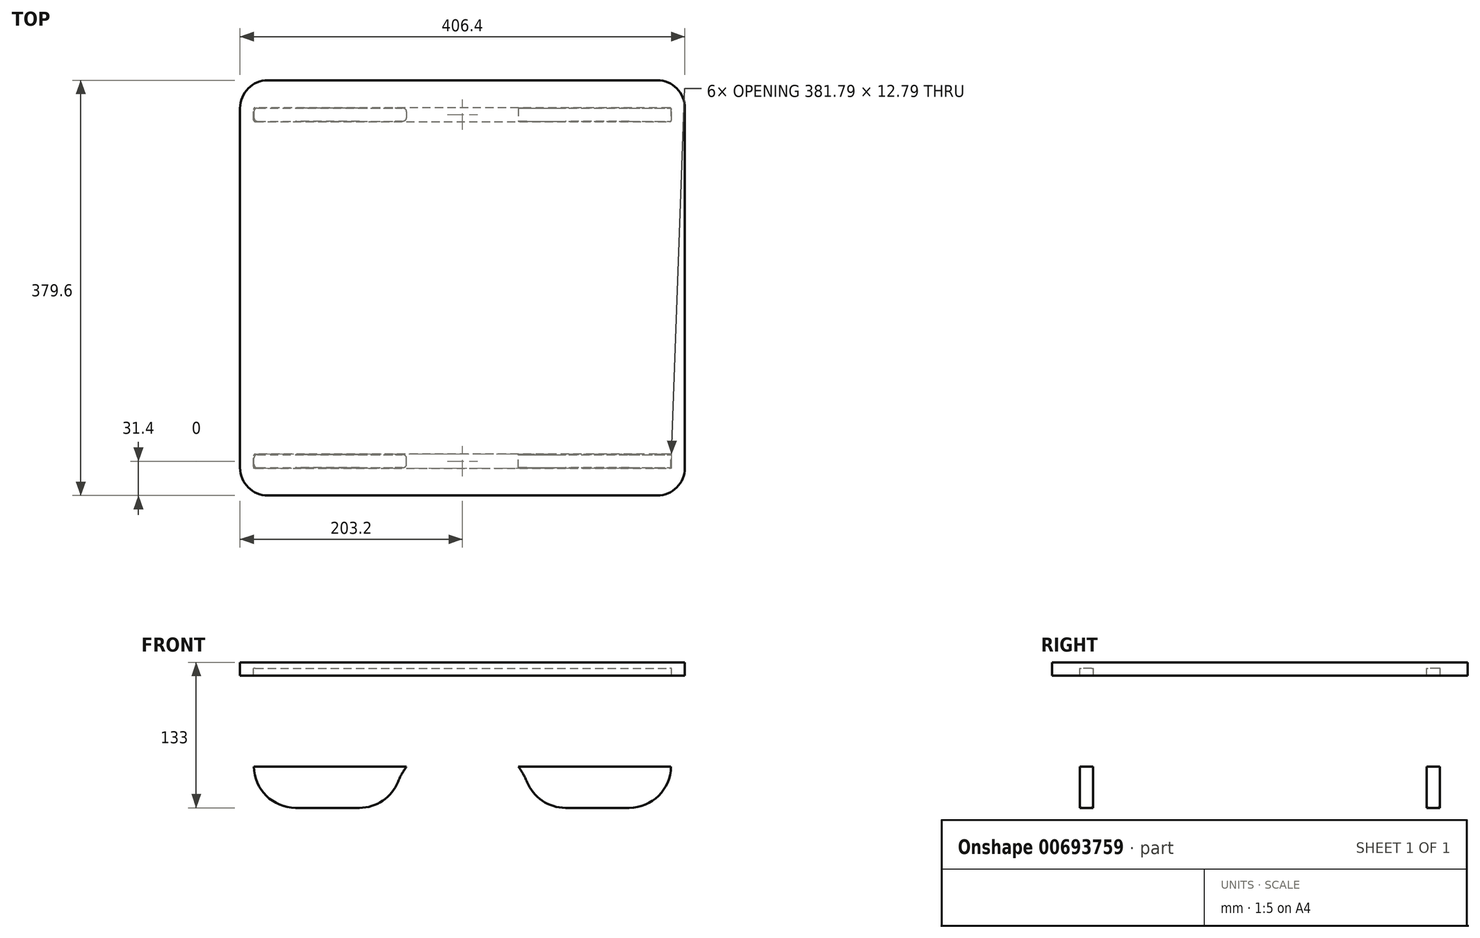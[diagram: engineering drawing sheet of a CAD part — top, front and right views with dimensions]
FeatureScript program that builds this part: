
annotation { "Feature Type Name" : "Feature", "Feature Type Description" : "" }
export const myFeature = defineFeature(function(context is Context, id is Id, definition is map)
    precondition{}
    {
        {
            var Q0;
            Q0=qCreatedBy(makeId("Front.planeOp"),FACE);
            var sketch = newSketch(context, id + "F0", { "sketchPlane" : qUnion([Q0])});
            skArc(sketch, "E0", {"start": v(-63.5, 0) * mm, "mid": v(0, 63.5) * mm, "end": v(63.5, 0) * mm});
            skLineSegment(sketch, "E1", {"start": v(-63.5, 0) * mm, "end": v(-190.5, 0) * mm});
            skLineSegment(sketch, "E2", {"start": v(-190.5, 0) * mm, "end": v(-190.5, 127) * mm});
            skLineSegment(sketch, "E3", {"start": v(-190.5, 127) * mm, "end": v(190.5, 127) * mm});
            skLineSegment(sketch, "E4", {"start": v(190.5, 127) * mm, "end": v(190.5, 0) * mm});
            skLineSegment(sketch, "E5", {"start": v(190.5, 0) * mm, "end": v(63.5, 0) * mm});
            skSolve(sketch);
        }
        {
            var Q0;
            Q0 = qSketchRegion(id + "F0", true);
            extrude(context, id + "F1", {"entities" : qUnion([Q0]), "oppositeDirection" : true, "depth" : 12 * mm, "offsetDistance" : 25.4 * mm});
        }
        {
            var Q0;
            Q0=makeQuery(id+"F1.opExtrude","SWEPT_EDGE",EDGE,{"disambiguationData":[OSD([sQuery(id+"F0.wireOp",EDGE,"E1"),sQuery(id+"F0.wireOp",EDGE,"E2")])]});
            var Q1;
            Q1=makeQuery(id+"F1.opExtrude","SWEPT_EDGE",EDGE,{"disambiguationData":[OSD([sQuery(id+"F0.wireOp",EDGE,"E0"),sQuery(id+"F0.wireOp",EDGE,"E1")])]});
            var Q2;
            Q2=makeQuery(id+"F1.opExtrude","SWEPT_EDGE",EDGE,{"disambiguationData":[OSD([sQuery(id+"F0.wireOp",EDGE,"E0"),sQuery(id+"F0.wireOp",EDGE,"E5")])]});
            var Q3;
            Q3=makeQuery(id+"F1.opExtrude","SWEPT_EDGE",EDGE,{"disambiguationData":[OSD([sQuery(id+"F0.wireOp",EDGE,"E4"),sQuery(id+"F0.wireOp",EDGE,"E5")])]});
            fillet(context, id + "F2", {"entities" : qUnion([Q0, Q1, Q2, Q3]), "radius" : 38.1 * mm, "tangentPropagation" : true, "allowEdgeOverflow" : false});
        }
        {
            var Q0;
            Q0=qCreatedBy(makeId("Front.planeOp"),FACE);
            cPlane(context, id + "F3", {"entities" : qUnion([Q0]), "cplaneType" : CPlaneType.OFFSET, "offset" : 304.8 * mm, "width" : 152.4 * mm, "height" : 152.4 * mm});
        }
        {
            var Q0;
            Q0=qCreatedBy(id+"F3.planeOp",FACE);
            var sketch = newSketch(context, id + "F4", { "sketchPlane" : qUnion([Q0])});
            skArc(sketch, "E6.0", {"start": v(-63.5, 0) * mm, "mid": v(0, 63.5) * mm, "end": v(63.5, 0) * mm});
            skLineSegment(sketch, "E6.1", {"start": v(-63.5, 0) * mm, "end": v(-190.5, 0) * mm});
            skLineSegment(sketch, "E6.2", {"start": v(-190.5, 0) * mm, "end": v(-190.5, 127) * mm});
            skLineSegment(sketch, "E6.3", {"start": v(-190.5, 127) * mm, "end": v(190.5, 127) * mm});
            skLineSegment(sketch, "E6.4", {"start": v(190.5, 127) * mm, "end": v(190.5, 0) * mm});
            skLineSegment(sketch, "E6.5", {"start": v(190.5, 0) * mm, "end": v(63.5, 0) * mm});
            skSolve(sketch);
        }
        {
            var Q0;
            Q0 = qSketchRegion(id + "F4", true);
            extrude(context, id + "F5", {"entities" : qUnion([Q0]), "depth" : 12 * mm, "offsetDistance" : 25.4 * mm});
        }
        {
            var Q0;
            Q0=makeQuery(id+"F5.opExtrude","SWEPT_EDGE",EDGE,{"disambiguationData":[OSD([sQuery(id+"F4.wireOp",EDGE,"E6.4"),sQuery(id+"F4.wireOp",EDGE,"E6.5")])]});
            var Q1;
            Q1=makeQuery(id+"F5.opExtrude","SWEPT_EDGE",EDGE,{"disambiguationData":[OSD([sQuery(id+"F4.wireOp",EDGE,"E6.0"),sQuery(id+"F4.wireOp",EDGE,"E6.1")])]});
            var Q2;
            Q2=makeQuery(id+"F5.opExtrude","SWEPT_EDGE",EDGE,{"disambiguationData":[OSD([sQuery(id+"F4.wireOp",EDGE,"E6.1"),sQuery(id+"F4.wireOp",EDGE,"E6.2")])]});
            var Q3;
            Q3=makeQuery(id+"F5.opExtrude","SWEPT_EDGE",EDGE,{"disambiguationData":[OSD([sQuery(id+"F4.wireOp",EDGE,"E6.0"),sQuery(id+"F4.wireOp",EDGE,"E6.5")])]});
            fillet(context, id + "F6", {"entities" : qUnion([Q0, Q1, Q2, Q3]), "radius" : 38.1 * mm, "tangentPropagation" : true, "allowEdgeOverflow" : false});
        }
        {
            var Q0;
            Q0=qCreatedBy(makeId("Right.planeOp"),FACE);
            var sketch = newSketch(context, id + "F7", { "sketchPlane" : qUnion([Q0])});
            skLineSegment(sketch, "E7.bottom", {"start": v(-342.2, 133) * mm, "end": v(37.4, 133) * mm});
            skLineSegment(sketch, "E7.top", {"start": v(-342.2, 121) * mm, "end": v(37.4, 121) * mm});
            skLineSegment(sketch, "E7.left", {"start": v(-342.2, 133) * mm, "end": v(-342.2, 121) * mm});
            skLineSegment(sketch, "E7.right", {"start": v(37.4, 133) * mm, "end": v(37.4, 121) * mm});
            skSolve(sketch);
        }
        {
            var Q0;
            Q0 = qSketchRegion(id + "F7", true);
            extrude(context, id + "F8", {"entities" : qUnion([Q0]), "endBound" : BoundingType.SYMMETRIC, "depth" : 406.4 * mm, "offsetDistance" : 25.4 * mm});
        }
        {
            var Q0;
            Q0=qCreatedBy(makeId("Right.planeOp"),FACE);
            var sketch = newSketch(context, id + "F9", { "sketchPlane" : qUnion([Q0])});
            skLineSegment(sketch, "E8.0", {"start": v(-317.2, 127.4) * mm, "end": v(-317.2, 37.7) * mm});
            skLineSegment(sketch, "E8.1", {"start": v(-304.4, 127.4) * mm, "end": v(-317.2, 127.4) * mm});
            skLineSegment(sketch, "E8.2", {"start": v(-304.4, 37.7) * mm, "end": v(-304.4, 127.4) * mm});
            skLineSegment(sketch, "E8.3", {"start": v(-317.2, 37.7) * mm, "end": v(-304.4, 37.7) * mm});
            skLineSegment(sketch, "E9.0", {"start": v(-0.4, 127.4) * mm, "end": v(-0.4, 37.7) * mm});
            skLineSegment(sketch, "E9.1", {"start": v(12.4, 127.4) * mm, "end": v(-0.4, 127.4) * mm});
            skLineSegment(sketch, "E9.2", {"start": v(12.4, 37.7) * mm, "end": v(12.4, 127.4) * mm});
            skLineSegment(sketch, "E9.3", {"start": v(-0.4, 37.7) * mm, "end": v(12.4, 37.7) * mm});
            skSolve(sketch);
        }
        {
            var Q0;
            Q0 = qSketchRegion(id + "F9", true);
            extrude(context, id + "F10", {"entities" : qUnion([Q0]), "operationType" : NewBodyOperationType.REMOVE, "endBound" : BoundingType.SYMMETRIC, "oppositeDirection" : true, "depth" : 381.8 * mm, "offsetDistance" : 25.4 * mm});
        }
        {
            var Q0;
            Q0=makeQuery(id+"F10.boolean.opBoolean","COPY",EDGE,{"derivedFrom":makeQuery(id+"F10.opExtrude","CAP_EDGE",EDGE,{"disambiguationData":[OSD([sQuery(id+"F9.wireOp",EDGE,"E8.0")])],"isStart":false})});
            var Q1;
            Q1=makeQuery(id+"F10.boolean.opBoolean","COPY",EDGE,{"derivedFrom":makeQuery(id+"F10.opExtrude","CAP_EDGE",EDGE,{"disambiguationData":[OSD([sQuery(id+"F9.wireOp",EDGE,"E8.2")])],"isStart":false})});
            var Q2;
            Q2=makeQuery(id+"F10.boolean.opBoolean","COPY",EDGE,{"derivedFrom":makeQuery(id+"F10.opExtrude","CAP_EDGE",EDGE,{"disambiguationData":[OSD([sQuery(id+"F9.wireOp",EDGE,"E8.0")])],"isStart":true})});
            var Q3;
            Q3=makeQuery(id+"F10.boolean.opBoolean","COPY",EDGE,{"derivedFrom":makeQuery(id+"F10.opExtrude","CAP_EDGE",EDGE,{"disambiguationData":[OSD([sQuery(id+"F9.wireOp",EDGE,"E8.2")])],"isStart":true})});
            var Q4;
            Q4=makeQuery(id+"F10.boolean.opBoolean","COPY",EDGE,{"derivedFrom":makeQuery(id+"F10.opExtrude","CAP_EDGE",EDGE,{"disambiguationData":[OSD([sQuery(id+"F9.wireOp",EDGE,"E9.0")])],"isStart":true})});
            var Q5;
            Q5=makeQuery(id+"F10.boolean.opBoolean","COPY",EDGE,{"derivedFrom":makeQuery(id+"F10.opExtrude","CAP_EDGE",EDGE,{"disambiguationData":[OSD([sQuery(id+"F9.wireOp",EDGE,"E9.2")])],"isStart":true})});
            var Q6;
            Q6=makeQuery(id+"F10.boolean.opBoolean","COPY",EDGE,{"derivedFrom":makeQuery(id+"F10.opExtrude","CAP_EDGE",EDGE,{"disambiguationData":[OSD([sQuery(id+"F9.wireOp",EDGE,"E9.0")])],"isStart":false})});
            var Q7;
            Q7=makeQuery(id+"F10.boolean.opBoolean","COPY",EDGE,{"derivedFrom":makeQuery(id+"F10.opExtrude","CAP_EDGE",EDGE,{"disambiguationData":[OSD([sQuery(id+"F9.wireOp",EDGE,"E9.2")])],"isStart":false})});
            fillet(context, id + "F11", {"entities" : qUnion([Q0, Q1, Q2, Q3, Q4, Q5, Q6, Q7]), "radius" : 1.59 * mm, "tangentPropagation" : true, "allowEdgeOverflow" : false});
        }
        {
            var Q0;
            Q0=makeQuery(id+"F1.opExtrude","CAP_EDGE",EDGE,{"disambiguationData":[OSD([sQuery(id+"F0.wireOp",EDGE,"E1")])],"isStart":true});
            var Q1;
            Q1=makeQuery(id+"F1.opExtrude","CAP_EDGE",EDGE,{"disambiguationData":[OSD([sQuery(id+"F0.wireOp",EDGE,"E1")])],"isStart":false});
            var Q2;
            {var subQ0=sQuery(id+"F4.wireOp",EDGE,"E6.1");var subQ1=sQuery(id+"F4.wireOp",EDGE,"E6.0");Q2=makeQuery(id+"F6.opFillet","BLEND_EDGE",EDGE,{"blendedFrom":[makeQuery(id+"F5.opExtrude","SWEPT_EDGE",EDGE,{"disambiguationData":[OSD([subQ1,subQ0])]}),makeQuery(id+"F5.opExtrude","CAP_FACE",FACE,{"disambiguationData":[OSD([subQ1,subQ0,sQuery(id+"F4.wireOp",EDGE,"E6.2"),sQuery(id+"F4.wireOp",EDGE,"E6.3"),sQuery(id+"F4.wireOp",EDGE,"E6.4"),sQuery(id+"F4.wireOp",EDGE,"E6.5")])],"isStart":false})],"blendedInto":[makeQuery(id+"F5.opExtrude","CAP_FACE",FACE,{"disambiguationData":[OSD([subQ1,subQ0,sQuery(id+"F4.wireOp",EDGE,"E6.2"),sQuery(id+"F4.wireOp",EDGE,"E6.3"),sQuery(id+"F4.wireOp",EDGE,"E6.4"),sQuery(id+"F4.wireOp",EDGE,"E6.5")])],"isStart":false})]});}
            var Q3;
            {var subQ0=sQuery(id+"F4.wireOp",EDGE,"E6.1");var subQ1=sQuery(id+"F4.wireOp",EDGE,"E6.0");Q3=makeQuery(id+"F6.opFillet","BLEND_EDGE",EDGE,{"blendedFrom":[makeQuery(id+"F5.opExtrude","SWEPT_EDGE",EDGE,{"disambiguationData":[OSD([subQ1,subQ0])]}),makeQuery(id+"F5.opExtrude","CAP_FACE",FACE,{"disambiguationData":[OSD([subQ1,subQ0,sQuery(id+"F4.wireOp",EDGE,"E6.2"),sQuery(id+"F4.wireOp",EDGE,"E6.3"),sQuery(id+"F4.wireOp",EDGE,"E6.4"),sQuery(id+"F4.wireOp",EDGE,"E6.5")])],"isStart":true})],"blendedInto":[makeQuery(id+"F5.opExtrude","CAP_FACE",FACE,{"disambiguationData":[OSD([subQ1,subQ0,sQuery(id+"F4.wireOp",EDGE,"E6.2"),sQuery(id+"F4.wireOp",EDGE,"E6.3"),sQuery(id+"F4.wireOp",EDGE,"E6.4"),sQuery(id+"F4.wireOp",EDGE,"E6.5")])],"isStart":true})]});}
            fillet(context, id + "F12", {"entities" : qUnion([Q0, Q1, Q2, Q3]), "radius" : 3.17 * mm, "tangentPropagation" : true, "allowEdgeOverflow" : false});
        }
        {
            var Q0;
            Q0=makeQuery(id+"F8.opExtrude","CAP_EDGE",EDGE,{"disambiguationData":[OSD([sQuery(id+"F7.wireOp",EDGE,"E7.left")])],"isStart":false});
            var Q1;
            Q1=makeQuery(id+"F8.opExtrude","CAP_EDGE",EDGE,{"disambiguationData":[OSD([sQuery(id+"F7.wireOp",EDGE,"E7.left")])],"isStart":true});
            var Q2;
            Q2=makeQuery(id+"F8.opExtrude","CAP_EDGE",EDGE,{"disambiguationData":[OSD([sQuery(id+"F7.wireOp",EDGE,"E7.right")])],"isStart":false});
            var Q3;
            Q3=makeQuery(id+"F8.opExtrude","CAP_EDGE",EDGE,{"disambiguationData":[OSD([sQuery(id+"F7.wireOp",EDGE,"E7.right")])],"isStart":true});
            fillet(context, id + "F13", {"entities" : qUnion([Q0, Q1, Q2, Q3]), "radius" : 25.4 * mm, "tangentPropagation" : true, "allowEdgeOverflow" : false});
        }
    });
